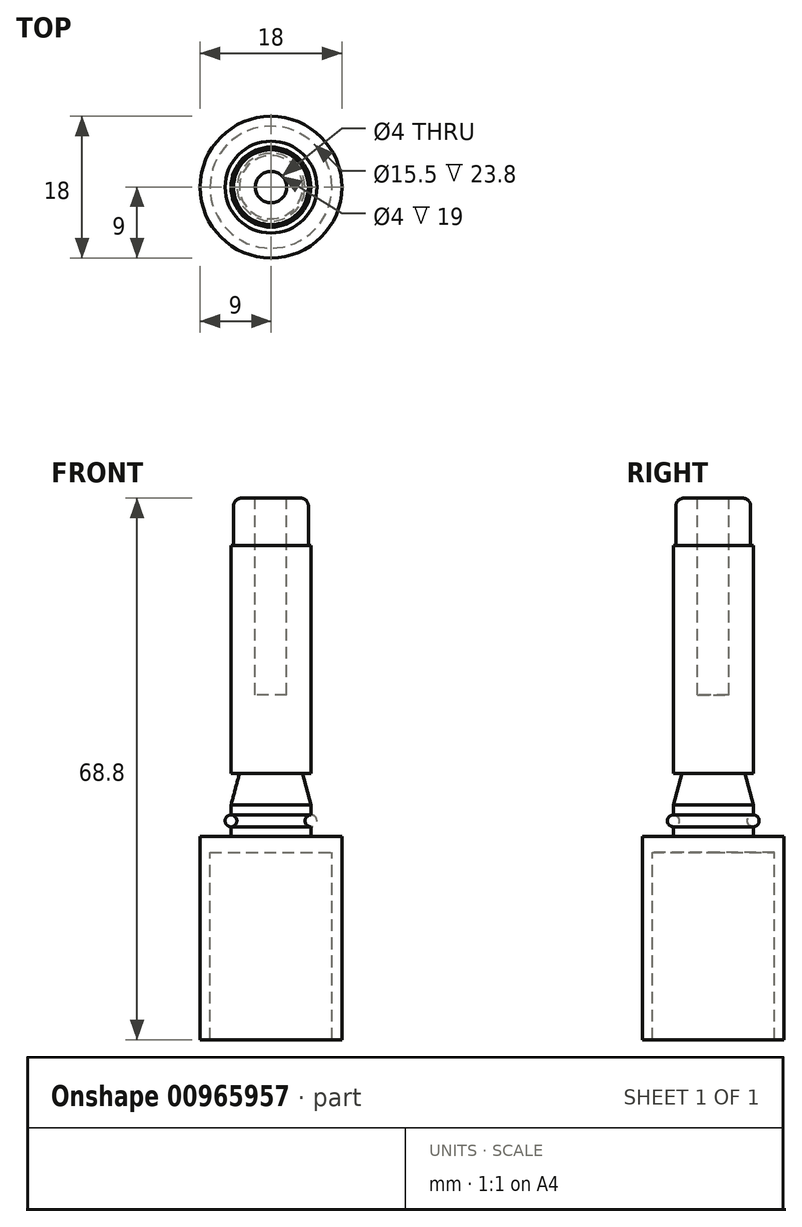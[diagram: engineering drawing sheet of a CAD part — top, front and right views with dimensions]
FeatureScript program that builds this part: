
annotation { "Feature Type Name" : "Feature", "Feature Type Description" : "" }
export const myFeature = defineFeature(function(context is Context, id is Id, definition is map)
    precondition{}
    {
        {
            var Q0;
            Q0=qCreatedBy(makeId("Top.planeOp"),FACE);
            var sketch = newSketch(context, id + "F0", { "sketchPlane" : qUnion([Q0])});
            skCircle(sketch, "E0", {"center": v(0, 0) * mm, "radius": 5.08 * mm});
            skSolve(sketch);
        }
        {
            var Q0;
            Q0=makeQuery(id+"F0.imprint","IMPRINT",FACE,{"disambiguationData":[TD([[makeQuery(id+"F0.imprint","IMPRINT",EDGE,{"derivedFrom":sQuery(id+"F0.wireOp",EDGE,"E0")}),1.0]])]});
            extrude(context, id + "F1", {"entities" : qUnion([Q0]), "depth" : 37 * mm, "offsetDistance" : 25 * mm});
        }
        {
            var Q0;
            Q0=makeQuery(id+"F1.opExtrude","CAP_FACE",FACE,{"disambiguationData":[OSD([sQuery(id+"F0.wireOp",EDGE,"E0")])],"isStart":true});
            var sketch = newSketch(context, id + "F2", { "sketchPlane" : qUnion([Q0])});
            skCircle(sketch, "E1", {"center": v(0, 0) * mm, "radius": 9 * mm});
            skSolve(sketch);
        }
        {
            var Q0;
            Q0 = qSketchRegion(id + "F2", true);
            extrude(context, id + "F3", {"entities" : qUnion([Q0]), "operationType" : NewBodyOperationType.ADD, "depth" : 2 * mm, "offsetDistance" : 25 * mm});
        }
        {
            var Q0;
            Q0=makeQuery(id+"F3.opExtrude","CAP_FACE",FACE,{"disambiguationData":[OSD([sQuery(id+"F2.wireOp",EDGE,"E1")])],"isStart":false});
            var sketch = newSketch(context, id + "F4", { "sketchPlane" : qUnion([Q0])});
            skCircle(sketch, "E2", {"center": v(0, 0) * mm, "radius": 7.75 * mm});
            skCircle(sketch, "E3.0", {"center": v(0, 0) * mm, "radius": 9 * mm});
            skSolve(sketch);
        }
        {
            var Q0;
            Q0=makeQuery(id+"F4.imprint","IMPRINT",FACE,{"disambiguationData":[TD([[makeQuery(id+"F4.imprint","IMPRINT",EDGE,{"derivedFrom":sQuery(id+"F4.wireOp",EDGE,"E2")}),-1.0]])]});
            extrude(context, id + "F5", {"entities" : qUnion([Q0]), "operationType" : NewBodyOperationType.ADD, "depth" : 23.8 * mm, "offsetDistance" : 25 * mm});
        }
        {
            var Q0;
            Q0=makeQuery(id+"F1.opExtrude","CAP_FACE",FACE,{"disambiguationData":[OSD([sQuery(id+"F0.wireOp",EDGE,"E0")])],"isStart":false});
            var sketch = newSketch(context, id + "F6", { "sketchPlane" : qUnion([Q0])});
            skCircle(sketch, "E4.0", {"center": v(0, 0) * mm, "radius": 5.08 * mm, "construction": true});
            skCircle(sketch, "E5", {"center": v(0, 0) * mm, "radius": 4.75 * mm});
            skSolve(sketch);
        }
        {
            var Q0;
            Q0 = qSketchRegion(id + "F6", true);
            extrude(context, id + "F7", {"entities" : qUnion([Q0]), "depth" : 6 * mm, "offsetDistance" : 25 * mm});
        }
        {
            var Q0;
            Q0=makeQuery(id+"F7.opExtrude","CAP_EDGE",EDGE,{"disambiguationData":[OSD([sQuery(id+"F6.wireOp",EDGE,"E4.0")])],"isStart":false});
            var Q1;
            Q1=makeQuery(id+"F7.opExtrude","CAP_EDGE",EDGE,{"disambiguationData":[OSD([sQuery(id+"F6.wireOp",EDGE,"E5")])],"isStart":false});
            fillet(context, id + "F8", {"entities" : qUnion([Q0, Q1]), "radius" : 1 * mm, "tangentPropagation" : true, "allowEdgeOverflow" : false});
        }
        {
            var Q0;
            Q0=qCreatedBy(makeId("Front.planeOp"),FACE);
            var sketch = newSketch(context, id + "F9", { "sketchPlane" : qUnion([Q0])});
            skLineSegment(sketch, "E6", {"start": v(-5.08, 0) * mm, "end": v(-5.08, 37) * mm});
            skCircle(sketch, "E7", {"center": v(-5.08, 2) * mm, "radius": 0.75 * mm});
            skLineSegment(sketch, "E8", {"start": v(-5.08, 8) * mm, "end": v(-4, 8) * mm});
            skLineSegment(sketch, "E9", {"start": v(-4, 8) * mm, "end": v(-5.08, 4) * mm});
            skLineSegment(sketch, "E10", {"start": v(-5.08, 4) * mm, "end": v(-5.08, 8) * mm});
            skArc(sketch, "E11", {"start": v(-5.08, 9.5) * mm, "mid": v(-5.83, 8.75) * mm, "end": v(-5.08, 8) * mm});
            skLineSegment(sketch, "E12.0", {"start": v(9, 0) * mm, "end": v(-9, 0) * mm, "construction": true});
            skSolve(sketch);
        }
        {
            var Q0;
            Q0=makeQuery(id+"F9.imprint","IMPRINT",FACE,{"disambiguationData":[TD([[makeQuery(id+"F9.imprint","IMPRINT",EDGE,{"derivedFrom":sQuery(id+"F9.wireOp",EDGE,"E8")}),-1.0]])]});
            var Q1;
            Q1=makeQuery(id+"F1.opExtrude","SWEPT_FACE",FACE,{"disambiguationData":[OSD([sQuery(id+"F0.wireOp",EDGE,"E0")])]});
            revolve(context, id + "F10", {"operationType" : NewBodyOperationType.REMOVE, "surfaceOperationType" : NewSurfaceOperationType.NEW, "entities" : qUnion([Q0]), "axis" : qUnion([Q1]), "revolveType" : RevolveType.FULL, "oppositeDirection" : true});
        }
        {
            var Q0;
            {var subQ0=sQuery(id+"F9.wireOp",EDGE,"E7");var subQ1=sQuery(id+"F9.wireOp",EDGE,"E6");var subQ2=makeQuery(id+"F9.imprint","INTERSECT",VERTEX,{"disambiguationData":[OD(0.0)],"derivedFrom":[subQ1,subQ0]});Q0=makeQuery(id+"F9.imprint","IMPRINT",FACE,{"disambiguationData":[TD([[makeQuery(id+"F9.imprint","IMPRINT",EDGE,{"disambiguationData":[TD([[subQ2,-1.0]])],"derivedFrom":subQ1}),1.0]])]});}
            var Q1;
            {var subQ0=sQuery(id+"F9.wireOp",EDGE,"E7");var subQ1=sQuery(id+"F9.wireOp",EDGE,"E6");var subQ2=makeQuery(id+"F9.imprint","INTERSECT",VERTEX,{"disambiguationData":[OD(0.0)],"derivedFrom":[subQ1,subQ0]});Q1=makeQuery(id+"F9.imprint","IMPRINT",FACE,{"disambiguationData":[TD([[makeQuery(id+"F9.imprint","IMPRINT",EDGE,{"disambiguationData":[TD([[subQ2,-1.0]])],"derivedFrom":subQ1}),-1.0]])]});}
            var Q2;
            {var subQ0=sQuery(id+"F0.wireOp",EDGE,"E0");Q2=makeQuery(id+"F10.boolean.opBoolean","SPLIT",FACE,{"disambiguationData":[TD([makeQuery(id+"F1.opExtrude","CAP_FACE",FACE,{"disambiguationData":[OSD([subQ0])],"isStart":false})])],"derivedFrom":makeQuery(id+"F1.opExtrude","SWEPT_FACE",FACE,{"disambiguationData":[OSD([subQ0])]})});}
            revolve(context, id + "F11", {"operationType" : NewBodyOperationType.REMOVE, "surfaceOperationType" : NewSurfaceOperationType.NEW, "entities" : qUnion([Q0, Q1]), "axis" : qUnion([Q2]), "revolveType" : RevolveType.FULL});
        }
        {
            var Q0;
            {var subQ0=sQuery(id+"F9.wireOp",EDGE,"E7");var subQ1=sQuery(id+"F9.wireOp",EDGE,"E6");var subQ2=makeQuery(id+"F9.imprint","INTERSECT",VERTEX,{"disambiguationData":[OD(0.0)],"derivedFrom":[subQ1,subQ0]});Q0=makeQuery(id+"F9.imprint","IMPRINT",FACE,{"disambiguationData":[TD([[makeQuery(id+"F9.imprint","IMPRINT",EDGE,{"disambiguationData":[TD([[subQ2,-1.0]])],"derivedFrom":subQ1}),-1.0]])]});}
            var Q1;
            {var subQ0=sQuery(id+"F9.wireOp",EDGE,"E7");var subQ1=sQuery(id+"F9.wireOp",EDGE,"E6");var subQ2=makeQuery(id+"F9.imprint","INTERSECT",VERTEX,{"disambiguationData":[OD(0.0)],"derivedFrom":[subQ1,subQ0]});Q1=makeQuery(id+"F9.imprint","IMPRINT",FACE,{"disambiguationData":[TD([[makeQuery(id+"F9.imprint","IMPRINT",EDGE,{"disambiguationData":[TD([[subQ2,-1.0]])],"derivedFrom":subQ1}),1.0]])]});}
            var Q2;
            {var subQ0=sQuery(id+"F0.wireOp",EDGE,"E0");Q2=makeQuery(id+"F10.boolean.opBoolean","SPLIT",FACE,{"disambiguationData":[TD([makeQuery(id+"F1.opExtrude","CAP_FACE",FACE,{"disambiguationData":[OSD([subQ0])],"isStart":false})])],"derivedFrom":makeQuery(id+"F1.opExtrude","SWEPT_FACE",FACE,{"disambiguationData":[OSD([subQ0])]})});}
            revolve(context, id + "F12", {"surfaceOperationType" : NewSurfaceOperationType.NEW, "entities" : qUnion([Q0, Q1]), "axis" : qUnion([Q2]), "revolveType" : RevolveType.FULL});
        }
        {
            var Q0;
            Q0=makeQuery(id+"F7.opExtrude","CAP_FACE",FACE,{"disambiguationData":[OSD([sQuery(id+"F6.wireOp",EDGE,"E5")])],"isStart":false});
            var sketch = newSketch(context, id + "F13", { "sketchPlane" : qUnion([Q0])});
            skCircle(sketch, "E13", {"center": v(0, 0) * mm, "radius": 2 * mm});
            skSolve(sketch);
        }
        {
            var Q0;
            Q0=makeQuery(id+"F13.imprint","IMPRINT",FACE,{"disambiguationData":[TD([[makeQuery(id+"F13.imprint","IMPRINT",EDGE,{"derivedFrom":sQuery(id+"F13.wireOp",EDGE,"E13")}),1.0]])]});
            extrude(context, id + "F14", {"entities" : qUnion([Q0]), "operationType" : NewBodyOperationType.REMOVE, "oppositeDirection" : true, "depth" : 25 * mm, "offsetDistance" : 25 * mm});
        }
    });
